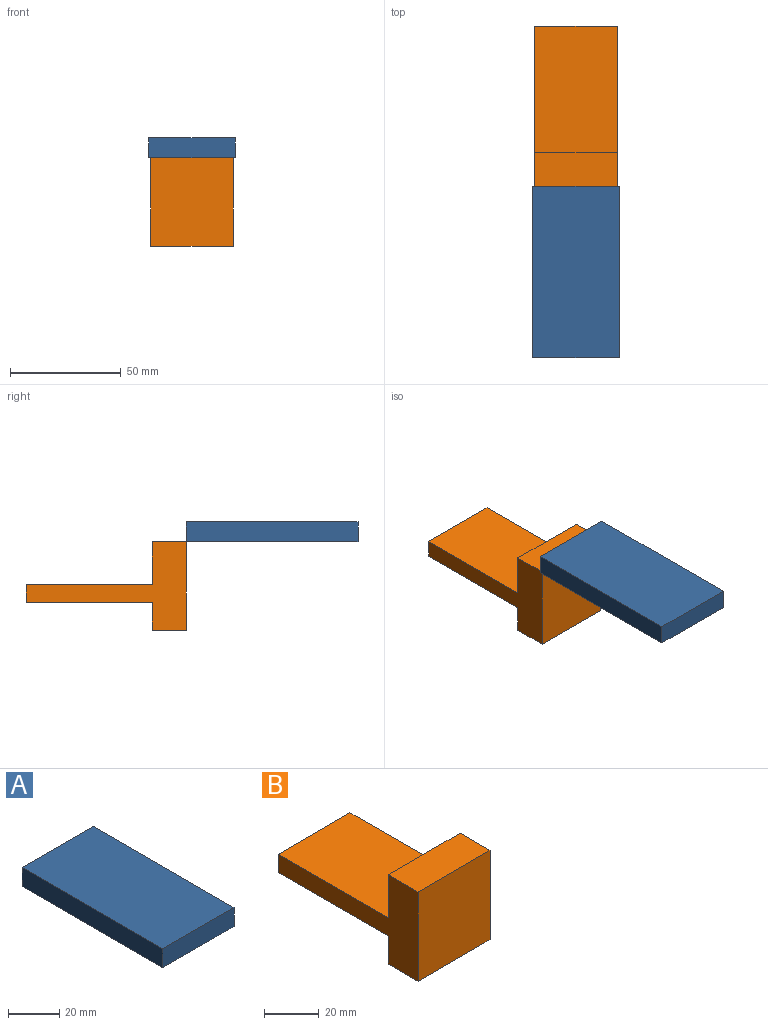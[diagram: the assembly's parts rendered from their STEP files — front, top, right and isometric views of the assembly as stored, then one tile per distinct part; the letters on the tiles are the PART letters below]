
ASSEMBLY  parts=2 mates=1
PART A: 6 faces, bbox 39.2x77.6x9 mm
  f0: plane 77.58x9mm, normal (-1,0,0), area 698.3mm2, adj f1,f3,f4,f5
  f1: plane 39.18x9mm, normal (0,-1,0), area 352.7mm2, adj f0,f2,f4,f5
  f2: plane 77.58x9mm, normal (1,0,0), area 698.3mm2, adj f1,f3,f4,f5
  f3: plane 39.18x9mm, normal (0,1,0), area 352.7mm2, adj f0,f2,f4,f5
  f4: plane 77.58x39.18mm, normal (0,0,1), area 3040.1mm2, adj f0,f1,f2,f3
  f5: plane 77.58x39.18mm, normal (0,0,-1), area 3040.1mm2, adj f0,f1,f2,f3
PART B: 10 faces, bbox 37.2x72.4x40 mm
  f0: plane 37.24x12.51mm, normal (0,1,0), area 466mm2, adj f2,f4,f6,f7
  f1: plane 40x37.24mm, normal (0,-1,0), area 1489.7mm2, adj f2,f4,f5,f6
  f2: plane 72.43x40mm, normal (1,0,0), area 1079.5mm2, adj f0,f1,f3,f5,f6,f7,f8,f9
  f3: plane 37.24x19.37mm, normal (0,1,0), area 721.6mm2, adj f2,f4,f5,f8
  f4: plane 72.43x40mm, normal (-1,0,0), area 1079.5mm2, adj f0,f1,f3,f5,f6,f7,f8,f9
  f5: plane 37.24x15.43mm, normal (0,0,1), area 574.5mm2, adj f1,f2,f3,f4
  f6: plane 37.24x15.43mm, normal (0,0,-1), area 574.5mm2, adj f0,f1,f2,f4
  f7: plane 57x37.24mm, normal (0,0,-1), area 2122.8mm2, adj f0,f2,f4,f9
  f8: plane 57x37.24mm, normal (0,0,1), area 2122.8mm2, adj f2,f3,f4,f9
  f9: plane 37.24x8.11mm, normal (0,1,0), area 302.2mm2, adj f2,f4,f7,f8
PLACE A t=(1.06,-22.79,83.41)mm
PLACE B t=(1.46,-31.33,43.41)mm
MATE parallel A.f5 <-> B.f5  axis (0,0,-1) through (9.19,11.37,83.41)mm
